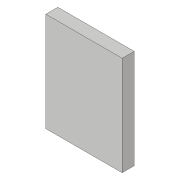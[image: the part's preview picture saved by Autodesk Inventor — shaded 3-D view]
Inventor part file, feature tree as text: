
AUTODESK INVENTOR PART (.ipt)
format: ipt  version: 2018.3 (Build 223284000, 284)  size: 71,680 bytes
history: native  units: in
note: dims shown in document units (in); Inventor stores cm internally (conversion verified against a paired STEP export)
features: extrude x1, sketch x1
ambient origin geometry x8: Origin, YZ Plane, XZ Plane, XY Plane, X Axis, Y Axis, Z Axis, Center Point
bodies: Solid1 (feature_tree)
feature tree (2):
  extrude  "Extrusion1"  Depth=2.56in
  sketch  "Sketch1"  dims[d0=1.97in d1=2.56in d2=0.31in d3=0.0in]
